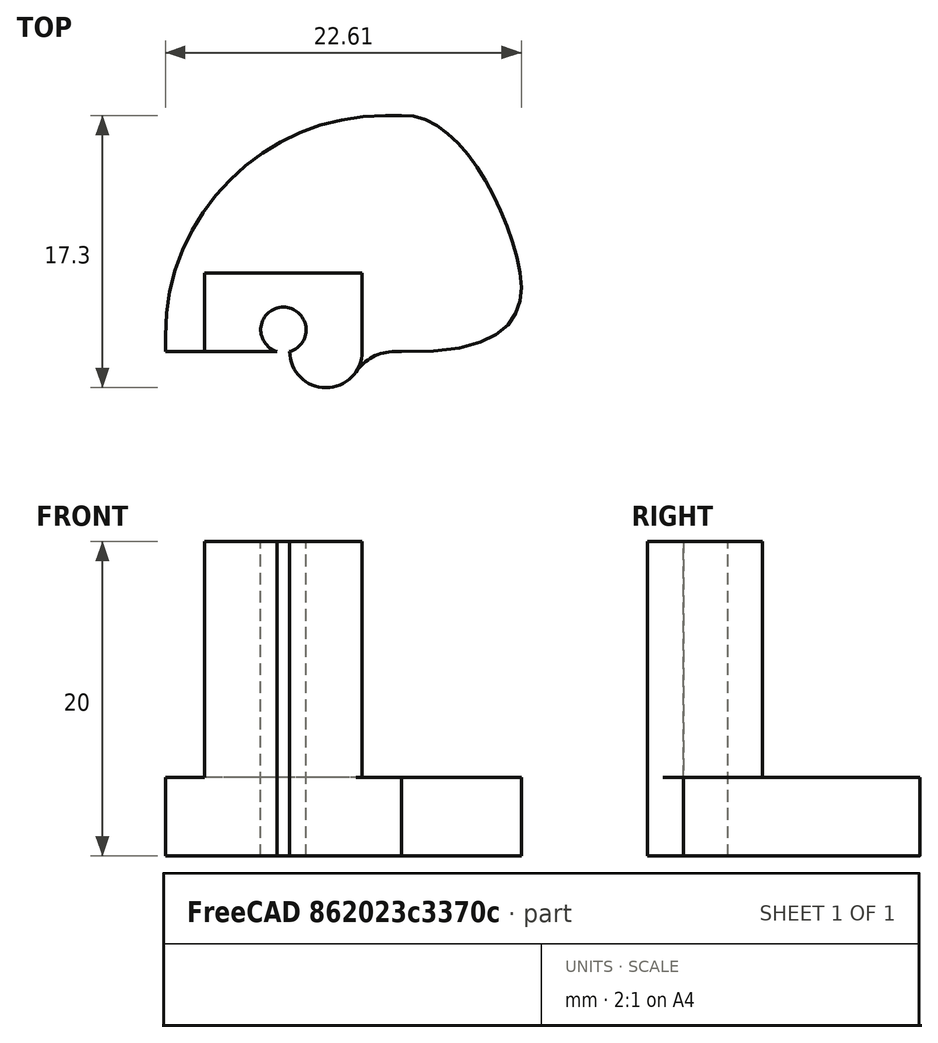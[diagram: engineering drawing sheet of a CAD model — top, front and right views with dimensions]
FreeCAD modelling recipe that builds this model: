
FCSTD DOCUMENT  (FreeCAD 0.18.1R)
Label: immortalT
License: All rights reserved
LicenseURL: http://en.wikipedia.org/wiki/All_rights_reserved
objects: Sketcher::SketchObject×6, Fem::FeaturePython×5, Fem::FemSolverObjectPython×4, App::MaterialObjectPython×3, Fem::ConstraintPython×3, PartDesign::Pad×2, PartDesign::AdditivePipe×2, PartDesign::Fillet×2, Mesh::Feature×2, PartDesign::Pocket×1, PartDesign::Body×1, Fem::ConstraintFixed×1, Fem::ConstraintFluidBoundary×1, Fem::FemMeshObjectPython×1, Fem::FemSetNodesObject×1, Fem::FemAnalysis×1
note: 19 computed .brp shape members not serialized (recipe doc carries the construction recipe); baked Part::Feature solids carry a one-line shape summary decoded from their .brp

FEATURE [Sketcher::SketchObject] Sketch
  MapMode = 5
  Support = -> [XY_Plane]
  sketch-geometry (4):
    g0: LineSegment StartX=0 StartY=0 StartZ=0 EndX=15 EndY=0 EndZ=0
    g1: LineSegment StartX=15 StartY=0 StartZ=0 EndX=15 EndY=15 EndZ=0
    g2: LineSegment StartX=15 StartY=15 StartZ=0 EndX=0 EndY=15 EndZ=0
    g3: LineSegment StartX=0 StartY=15 StartZ=0 EndX=0 EndY=0 EndZ=0
  constraints (11):
    c: Coincident(g0,g1)
    c: Coincident(g1,g2)
    c: Coincident(g2,g3)
    c: Coincident(g3,g0)
    c: Horizontal(g0)
    c: Horizontal(g2)
    c: Vertical(g1)
    c: Vertical(g3)
    c: Coincident(g0,g-1)
    c: DistanceX(g2,g2) = 15
    c: DistanceY(g3,g3) = 15
FEATURE [PartDesign::Pad] Pad
  Length = 5
  Length2 = 100
  Profile = -> Sketch
  Refine = true
  Type = 0
FEATURE [Sketcher::SketchObject] Sketch001
  ExternalGeometry = -> [Pad]
  MapMode = 5
  Placement = pos=(0,0,5) rot=(0,0,1;0rad)
  Support = -> [Pad]
  sketch-geometry (4):
    g0: LineSegment StartX=2.5 StartY=0 StartZ=0 EndX=12.5 EndY=0 EndZ=0
    g1: LineSegment StartX=12.5 StartY=0 StartZ=0 EndX=12.5 EndY=5 EndZ=0
    g2: LineSegment StartX=12.5 StartY=5 StartZ=0 EndX=2.5 EndY=5 EndZ=0
    g3: LineSegment StartX=2.5 StartY=5 StartZ=0 EndX=2.5 EndY=0 EndZ=0
  constraints (12):
    c: Coincident(g0,g1)
    c: Coincident(g1,g2)
    c: Coincident(g2,g3)
    c: Coincident(g3,g0)
    c: Horizontal(g0)
    c: Horizontal(g2)
    c: Vertical(g1)
    c: Vertical(g3)
    c: PointOnObject(g0,g-3)
    c: DistanceX(g2,g2) = 10
    c: DistanceX(g-1,g0) = 2.5
    c: DistanceY(g3,g3) = 5
FEATURE [PartDesign::Pad] Pad001
  BaseFeature = -> Pad
  Length = 15
  Length2 = 100
  Profile = -> Sketch001
  Refine = true
  Type = 0
FEATURE [Sketcher::SketchObject] Sketch002
  ExternalGeometry = -> [Pad001]
  MapMode = 5
  Placement = pos=(0,0,20) rot=(0,0,1;0rad)
  Support = -> [Pad001]
  sketch-geometry (2):
    g0: ArcOfCircle CenterX=7.5 CenterY=1.38333 CenterZ=0 NormalX=0 NormalY=0 NormalZ=1 AngleXU=0 Radius=1.44 StartAngle=4.99387 EndAngle=10.7141
    g1: LineSegment StartX=7.1 StartY=3.11e-14 StartZ=0 EndX=7.9 EndY=3.09e-14 EndZ=0
  constraints (7):
    c: PointOnObject(g0,g-3)
    c: PointOnObject(g0,g-3)
    c: DistanceX(g-4,g0) = 5
    c: Radius(g0) = 1.44
    c: Coincident(g1,g0)
    c: Coincident(g1,g0)
    c: DistanceX(g0,g0) = 0.8
FEATURE [PartDesign::Pocket] Pocket
  BaseFeature = -> Pad001
  Length = 0
  Length2 = 100
  Profile = -> Sketch002
  Refine = true
  Type = 3
  UpToFace = -> Pad001 [Face2]
FEATURE [Sketcher::SketchObject] Sketch003
  ExternalGeometry = -> [Pocket]
  MapMode = 5
  Placement = pos=(0,0,0) rot=(1,0,0;3.14159rad)
  Support = -> [Pocket]
  sketch-geometry (10):
    g0: LineSegment StartX=15 StartY=0 StartZ=0 EndX=15 EndY=-15 EndZ=0
    g1-g5: Circle [constr] x5 (B-spline internal-alignment scaffolding for g6; pole/knot coordinates omitted)
    g6: BSplineCurve PolesCount=5 KnotsCount=3 Degree=3 IsPeriodic=0
    g7: GeomPoint [constr] X=15 Y=0 Z=0
    g8: GeomPoint [constr] X=21.885 Y=-7.465 Z=0
    g9: GeomPoint [constr] X=15 Y=-15 Z=0
  constraints (16):
    c: Coincident(g6,g0)
    c: Radius(g1) = 0.5
    c: Equal(g1, g2-g5) x4
    c: Coincident(g6,g0)
    c: InternalAlignment(g1-g5 -> g6) x5
    c: InternalAlignment(g7,g6)
    c: InternalAlignment(g8,g6)
    c: InternalAlignment(g9,g6)
    c: Coincident(g0,g-6)
    c: Coincident(g0,g-5)
    c: DistanceX(g0,g2) = 8.5
    c: DistanceY(g3,g2) = 7.69
    c: DistanceX(g0,g3) = 8.01
    c: DistanceY(g4,g0) = 15.11
    c: DistanceX(g0,g4) = 3.02
    c: DistanceY(g4,g3) = 7.63
FEATURE [PartDesign::AdditivePipe] AdditivePipe
  AuxilleryCurvelinear = true
  AuxillerySpineTangent = false
  BaseFeature = -> Pocket
  Binormal = (0,0,0)
  Mode = 0
  Profile = -> Sketch003
  Refine = true
  Spine = -> Pocket [Edge1]
  SpineTangent = false
  Transformation = 0
  Transition = 0
FEATURE [Sketcher::SketchObject] Sketch005
  ExternalGeometry = -> [AdditivePipe]
  MapMode = 5
  Placement = pos=(0,0,0) rot=(1,0,0;3.14159rad)
  Support = -> [AdditivePipe]
  sketch-geometry (2):
    g0: ArcOfCircle CenterX=10.2 CenterY=0 CenterZ=0 NormalX=0 NormalY=0 NormalZ=1 AngleXU=0 Radius=2.3 StartAngle=0 EndAngle=3.14159
    g1: LineSegment StartX=7.9 StartY=0 StartZ=0 EndX=12.5 EndY=0 EndZ=0
  constraints (6):
    c: Coincident(g1,g0)
    c: Coincident(g1,g0)
    c: PointOnObject(g0,g-3)
    c: Coincident(g0,g-3)
    c: Radius(g0) = 2.3
    c: Horizontal(g1)
FEATURE [Sketcher::SketchObject] Sketch006
  ExternalGeometry = -> [Sketch005,AdditivePipe]
  MapMode = 5
  Placement = pos=(0,0,0) rot=(1,0,0;1.5708rad)
  Support = -> [AdditivePipe]
  sketch-geometry (1):
    g0: LineSegment StartX=12.5 StartY=20 StartZ=0 EndX=12.5 EndY=0 EndZ=0
  constraints (2):
    c: Coincident(g0,g-3)
    c: Coincident(g0,g-5)
FEATURE [PartDesign::AdditivePipe] AdditivePipe001
  AuxilleryCurvelinear = true
  AuxillerySpineTangent = false
  BaseFeature = -> AdditivePipe
  Binormal = (0,0,0)
  Mode = 0
  Profile = -> Sketch005
  Refine = true
  Spine = -> Sketch006
  SpineTangent = false
  Transformation = 0
  Transition = 0
FEATURE [PartDesign::Fillet] Fillet
  Base = -> AdditivePipe001 [Edge1]
  BaseFeature = -> AdditivePipe001
  Radius = 3
FEATURE [PartDesign::Fillet] Fillet001
  Base = -> Fillet [Edge26]
  BaseFeature = -> Fillet
  Radius = 14
FEATURE [PartDesign::Body] Body
  Group = -> [Sketch,Pad,Sketch001,Pad001,Sketch002,Pocket,Sketch003,AdditivePipe,Sketch005,Sketch006,AdditivePipe001,Fillet,Fillet001]
  Origin = -> Origin
  Tip = -> Fillet001
FEATURE [Mesh::Feature] Mesh  label="Fillet001 (Meshed)"
FEATURE [Fem::FemSolverObjectPython] CalculiXccxTools  # FEM object (typed FeaturePython)
  AnalysisType = 0
  BeamShellResultOutput3D = false
  EigenmodeHighLimit = 1000000
  EigenmodeLowLimit = 0
  EigenmodesCount = 10
  GeometricalNonlinearity = 0
  IterationsControlParameterCutb = 0.25,0.5,0.75,0.85,,,1.5,
  IterationsControlParameterIter = 4,8,9,200,10,400,,200,,
  IterationsControlParameterTimeUse = false
  IterationsThermoMechMaximum = 200
  IterationsUserDefinedIncrementations = false
  IterationsUserDefinedTimeStepLength = false
  MaterialNonlinearity = 0
  MatrixSolverType = 0
  SplitInputWriter = false
  ThermoMechSteadyState = true
  TimeEnd = 1
  TimeInitialStep = 1
FEATURE [App::MaterialObjectPython] SolidMaterial  # material (typed FeaturePython)
  Category = 0
  Material = Density=1240 kg/m^3,+12 more (map truncated)
  References = -> [Fillet001]
FEATURE [App::MaterialObjectPython] FluidMaterial  # material (typed FeaturePython)
  Category = 1
  Material = Density=1.20 kg/m^3,Description=Standard air properties at 20 Degrees Celsius and 1 atm,DynamicViscosity=1.80e-5 kg/m/s,+8 more (map truncated)
  References = -> [Fillet001]
FEATURE [Fem::ConstraintFixed] FemConstraintFixed
  NormalDirection = (0,0,-1)
  Normals = (1) [(0,0,-1)]
  Points = (1) [(11.75,6.405,0)]
  References = -> [Fillet001]
FEATURE [Fem::FeaturePython] ElementFluid1D  # FEM object (typed FeaturePython)
  BendAngle = 0
  BendLossCoefficient = 0
  BendPipeArea = 20
  BendRadiusDiameter = 1
  ChannelSectionType = 0
  ColebrookeArea = 20
  ColebrookeFormFactor = 1
  ColebrookeGrainDiameter = 0.0025
  ColebrookeRadius = 1
  ContractArea1 = 20
  ContractArea2 = 10
  DiaphragmArea = 20
  DiaphragmPipeArea = 20
  EnlargeArea1 = 10
  EnlargeArea2 = 20
  EntranceArea = 20
  EntrancePipeArea = 20
  GasSectionType = 0
  GateValveClosingCoeff = 0.125
  GateValvePipeArea = 20
  InletFlowRate = 1
  InletFlowRateActive = false
  InletPressure = 1
  InletPressureActive = true
  LiquidSectionType = 3
  ManningArea = 10
  ManningCoefficient = 0.0015
  ManningRadius = 1
  OutletFlowRate = 1
  OutletFlowRateActive = false
  OutletPressure = 1
  OutletPressureActive = true
  PumpFlowRate = [0,0.000104,0.000208,0.000313,0.000417]
  PumpHeadLoss = [30,29.17,26.67,23.33,18.33]
  SectionType = 0
FEATURE [Fem::ConstraintPython] ConstraintInitialFlowVelocity  # FEM object (typed FeaturePython)
  NormalDirection = (0,0,1)
  VelocityX = 8.33333
  VelocityXEnabled = true
  VelocityY = 0
  VelocityYEnabled = false
  VelocityZ = 0
  VelocityZEnabled = false
FEATURE [Fem::ConstraintFluidBoundary] FluidBoundary
  BoundaryType = 4
  BoundaryValue = 0
  DirectionVector = (0.941575,0.336804,0)
  HTCoeffValue = 0
  HeatFluxValue = 0
  NormalDirection = (0.941575,0.336804,0)
  Normals = (52) [(-0.0363997,0.999337,0),(0.941575,0.336804,0),(-0.0246983,-0.999695,0),(-0.0363997,0.999337,0),(0.941575,0.336804,0),(-0.0246983,-0.999695,0),+46 more]
  Points = (52) [(15,15,5),(21.885,7.465,5),(15,0,5),(15,15,2.5),(21.885,7.465,2.5),(15,0,2.5),(15,15,0),(21.885,7.465,0),(15,0,0),(12.5,4.44e-15,20),(10.2,-2.3,20),+41 more]
  References = -> [Fillet001]
  Subtype = 1
  TemperatureValue = 0
  ThermalBoundaryType = 1
  TurbulenceSpecification = 1
  TurbulentIntensityValue = 0
  TurbulentLengthValue = 0
FEATURE [Fem::ConstraintPython] ConstraintFlowVelocity  # FEM object (typed FeaturePython)
  NormalDirection = (0.941575,0.336804,0)
  NormalToBoundary = false
  References = -> [Fillet001]
  VelocityX = 8
  VelocityXEnabled = true
  VelocityY = 0
  VelocityYEnabled = false
  VelocityZ = 0
  VelocityZEnabled = false
FEATURE [App::MaterialObjectPython] SolidMaterial001  # material (typed FeaturePython)
  Category = 0
  Material = Density=1240 kg/m^3,+12 more (map truncated)
  References = -> [Fillet001]
FEATURE [Fem::ConstraintPython] ConstraintSelfWeight  # FEM object (typed FeaturePython)
  Gravity_x = 0
  Gravity_y = 0
  Gravity_z = -1
  NormalDirection = (0,0,1)
FEATURE [Fem::FeaturePython] MeshBoundaryLayer  # FEM object (typed FeaturePython)
  GrowthRate = 1.5
  MinimumThickness = 0
  NumberOfLayers = 3
  References = -> [Fillet001]
FEATURE [Fem::FeaturePython] FEMMeshRegion  # FEM object (typed FeaturePython)
  CharacteristicLength = 0
  References = -> [Fillet001]
FEATURE [Mesh::Feature] Mesh001
FEATURE [Fem::FemSolverObjectPython] CalculiXccxTools001  # FEM object (typed FeaturePython)
  AnalysisType = 0
  BeamShellResultOutput3D = false
  EigenmodeHighLimit = 1000000
  EigenmodeLowLimit = 0
  EigenmodesCount = 10
  GeometricalNonlinearity = 0
  IterationsControlParameterCutb = 0.25,0.5,0.75,0.85,,,1.5,
  IterationsControlParameterIter = 4,8,9,200,10,400,,200,,
  IterationsControlParameterTimeUse = false
  IterationsThermoMechMaximum = 200
  IterationsUserDefinedIncrementations = false
  IterationsUserDefinedTimeStepLength = false
  MaterialNonlinearity = 0
  MatrixSolverType = 0
  SplitInputWriter = false
  ThermoMechSteadyState = true
  TimeEnd = 1
  TimeInitialStep = 1
FEATURE [Fem::FeaturePython] ElementGeometry1D  # FEM object (typed FeaturePython)
  CircDiameter = 25
  PipeDiameter = 25
  PipeThickness = 10
  RectHeight = 25
  RectWidth = 10
  SectionType = 0
FEATURE [Fem::FeaturePython] FEMMeshRegion001  # FEM object (typed FeaturePython)
  CharacteristicLength = 0
  References = -> [Fillet001]
FEATURE [Fem::FemMeshObjectPython] FEMMeshGmsh  # FEM object (typed FeaturePython)
  Algorithm2D = 0
  Algorithm3D = 0
  CharacteristicLengthMax = 0
  CharacteristicLengthMin = 0
  CoherenceMesh = true
  ElementDimension = 2
  ElementOrder = 1
  GeometryTolerance = 1e-06
  GroupsOfNodes = false
  HighOrderOptimize = false
  MeshRegionList = -> [FEMMeshRegion001]
  OptimizeNetgen = false
  OptimizeStd = true
  Part = -> Fillet001
  RecombineAll = false
FEATURE [Fem::FemSolverObjectPython] CalculiXccxTools002  # FEM object (typed FeaturePython)
  AnalysisType = 0
  BeamShellResultOutput3D = false
  EigenmodeHighLimit = 1000000
  EigenmodeLowLimit = 0
  EigenmodesCount = 10
  GeometricalNonlinearity = 0
  IterationsControlParameterCutb = 0.25,0.5,0.75,0.85,,,1.5,
  IterationsControlParameterIter = 4,8,9,200,10,400,,200,,
  IterationsControlParameterTimeUse = false
  IterationsThermoMechMaximum = 200
  IterationsUserDefinedIncrementations = false
  IterationsUserDefinedTimeStepLength = false
  MaterialNonlinearity = 0
  MatrixSolverType = 0
  SplitInputWriter = false
  ThermoMechSteadyState = true
  TimeEnd = 1
  TimeInitialStep = 1
FEATURE [Fem::FemSetNodesObject] NodesSet
  FemMesh = -> FEMMeshGmsh
FEATURE [Fem::FemSolverObjectPython] CalculiXccxTools003  # FEM object (typed FeaturePython)
  AnalysisType = 0
  BeamShellResultOutput3D = false
  EigenmodeHighLimit = 1000000
  EigenmodeLowLimit = 0
  EigenmodesCount = 10
  GeometricalNonlinearity = 0
  IterationsControlParameterCutb = 0.25,0.5,0.75,0.85,,,1.5,
  IterationsControlParameterIter = 4,8,9,200,10,400,,200,,
  IterationsControlParameterTimeUse = false
  IterationsThermoMechMaximum = 200
  IterationsUserDefinedIncrementations = false
  IterationsUserDefinedTimeStepLength = false
  MaterialNonlinearity = 0
  MatrixSolverType = 0
  SplitInputWriter = false
  ThermoMechSteadyState = true
  TimeEnd = 1
  TimeInitialStep = 1
FEATURE [Fem::FemAnalysis] Analysis
  Group = -> [CalculiXccxTools,SolidMaterial,FluidMaterial,FemConstraintFixed,ElementFluid1D,ConstraintInitialFlowVelocity,FluidBoundary,ConstraintFlowVelocity,SolidMaterial001,ConstraintSelfWeight,FEMMeshGmsh,CalculiXccxTools001,ElementGeometry1D,CalculiXccxTools002,CalculiXccxTools003]
